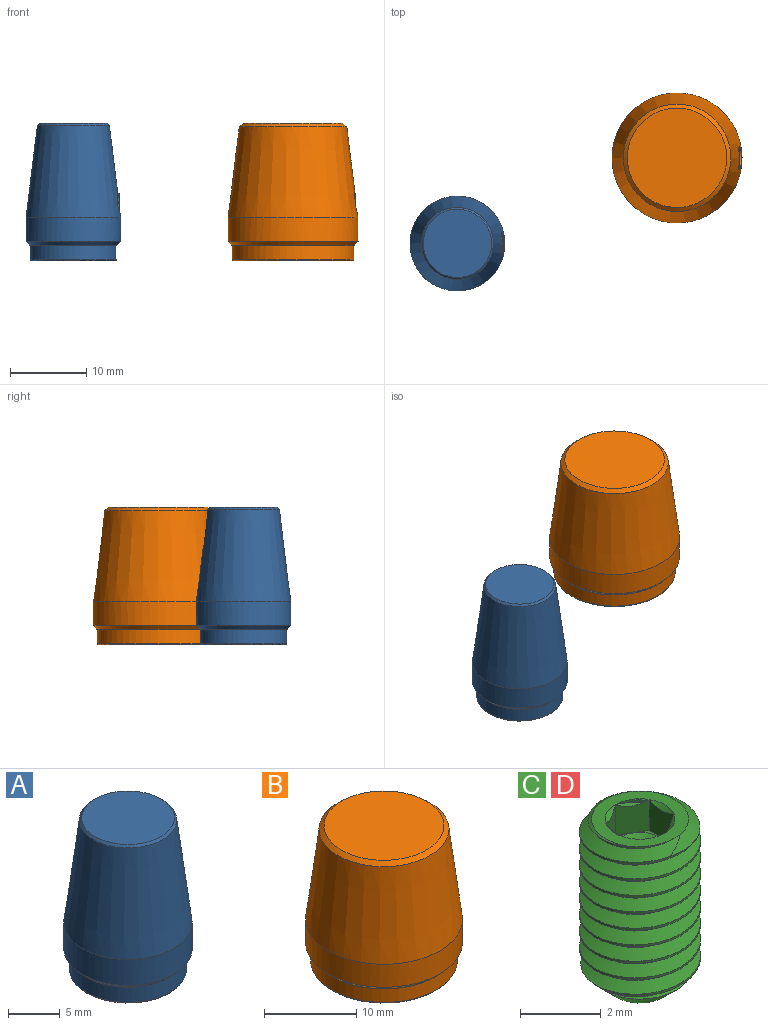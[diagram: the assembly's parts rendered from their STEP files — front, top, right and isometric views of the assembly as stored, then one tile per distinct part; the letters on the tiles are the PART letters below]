
ASSEMBLY  parts=4 mates=3
PART A: 20 faces, bbox 12.4x12.4x18 mm
  f0: cylinder r=1.61mm len=9.65mm, axis (0,0,-1), area 92.2mm2, adj f10,f12,f17
  f1: cone r=4.68mm half-angle=7deg, axis (0,0,-1), area 411.9mm2, adj f8,f11,f18
  f2: plane 8.96x8.96mm, normal (0,0,1), area 63mm2, adj f11
  f3: plane 1.22x1.22mm, normal (0,0,-1), area 1.2mm2, adj f10
  f4: plane 9.2x9.2mm, normal (0,0,-1), area 56.6mm2, adj f12,f13
  f5: cylinder r=4.75mm len=9.5mm, axis (0,0,-1), area 86.4mm2, adj f13,f14
  f6: plane 11x11mm, normal (0,0,-1), area 19.4mm2, adj f14,f15
  f7: cylinder r=5.65mm len=11.3mm, axis (0,0,-1), area 63.3mm2, adj f15,f16
  f8: cylinder r=6.2mm len=12.4mm, axis (0,0,-1), area 118.8mm2, adj f1,f9
  f9: cone r=5.65mm half-angle=45deg, axis (0,0,1), area 26.7mm2, adj f8,f16
  f10: cone r=0.61mm half-angle=45deg, axis (0,0,-1), area 9.9mm2, adj f0,f3
  f11: cone r=4.71mm half-angle=42.9deg, axis (0,0,-1), area 9.8mm2, adj f1,f2
  f12: torus R=1.76mm, axis (0,0,-1), area 2.5mm2, adj f0,f4
  f13: torus R=4.6mm, axis (0,0,-1), area 7.1mm2, adj f4,f5
  f14: torus R=4.9mm, axis (0,0,-1), area 7.2mm2, adj f5,f6
  f15: torus R=5.5mm, axis (0,0,-1), area 8.4mm2, adj f6,f7
  f16: torus R=5.8mm, axis (0,0,-1), area 4.3mm2, adj f7,f9
  f17: cylinder r=1.25mm len=3.69mm, axis (1,0,0), area 26.5mm2, adj f0,f19
  f18: cylinder r=1.55mm len=3.1mm, axis (1,0,0), area 11.2mm2, adj f1,f19
  f19: plane 3.1x3.1mm, normal (1,0,0), area 2.6mm2, adj f17,f18
PART B: 21 faces, bbox 17.5x17.5x18 mm
  f0: cone r=6.98mm half-angle=7deg, axis (0,0,-1), area 579.1mm2, adj f8,f11,f17
  f1: plane 13.02x13.02mm, normal (0,0,1), area 133mm2, adj f11
  f2: plane 1.22x1.22mm, normal (0,0,-1), area 1.2mm2, adj f10
  f3: cylinder r=1.61mm len=9.65mm, axis (0,0,-1), area 97.6mm2, adj f10,f12
  f4: plane 11.7x11.7mm, normal (0,0,-1), area 97.7mm2, adj f12,f13
  f5: cylinder r=6mm len=12mm, axis (0,0,-1), area 109.1mm2, adj f13,f14
  f6: plane 15.6x15.6mm, normal (0,0,-1), area 72.1mm2, adj f14,f15
  f7: cylinder r=7.95mm len=15.9mm, axis (0,0,-1), area 89.1mm2, adj f15,f16
  f8: cylinder r=8.5mm len=17mm, axis (0,0,-1), area 162.9mm2, adj f0,f9
  f9: cone r=7.95mm half-angle=45deg, axis (0,0,1), area 37mm2, adj f8,f16
  f10: cone r=0.61mm half-angle=45deg, axis (0,0,-1), area 9.9mm2, adj f2,f3
  f11: cone r=7.03mm half-angle=48.5deg, axis (0,0,-1), area 30mm2, adj f0,f1
  f12: torus R=1.76mm, axis (0,0,-1), area 2.5mm2, adj f3,f4
  f13: torus R=5.85mm, axis (0,0,-1), area 8.9mm2, adj f4,f5
  f14: torus R=6.15mm, axis (0,0,-1), area 9.1mm2, adj f5,f6
  f15: torus R=7.8mm, axis (0,0,-1), area 11.9mm2, adj f6,f7
  f16: torus R=8.1mm, axis (0,0,-1), area 6mm2, adj f7,f9
  f17: cylinder r=1.55mm len=3.1mm, axis (1,0,0), area 11.1mm2, adj f0,f19
  f18: cylinder r=1.25mm len=4mm, axis (1,0,0), area 31.4mm2, adj f19,f20
  f19: plane 3.1x3.1mm, normal (1,0,0), area 2.6mm2, adj f17,f18
  f20: cone r=0mm half-angle=59deg, axis (1,0,0), area 5.7mm2, adj f18
PART C: 27 faces, bbox 3.3x3.8x5.5 mm
  f0: cone r=0.75mm half-angle=60deg, axis (0,0,1), area 2mm2, adj f6,f7,f8,f9,f10,f20
  f1: cone r=0.87mm half-angle=45deg, axis (0,0,1), area 0.1mm2, adj f11,f25
  f2: cone r=1664.28mm half-angle=59deg, axis (0,0,-1), area 2.5mm2, adj f3
  f3: cone r=0.82mm half-angle=45deg, axis (0,0,1), area 5mm2, adj f2,f4,f12,f13,f14
  f4: cylinder r=1.5mm len=4.11mm, axis (0,0,1), area 4.8mm2, adj f3,f5,f12,f14
  f5: cone r=1.5mm half-angle=55deg, axis (0,0,-1), area 1.4mm2, adj f4,f11,f12,f14
  f6: plane 0.65x0.38mm, normal (0,0,1), area 0mm2, adj f0,f25,f26
  f7: plane 0.75x0.22mm, normal (0,0,1), area 0mm2, adj f0,f21,f26
  f8: plane 0.65x0.38mm, normal (0,0,1), area 0mm2, adj f0,f21,f22
  f9: plane 0.65x0.38mm, normal (0,0,1), area 0mm2, adj f0,f22,f23
  f10: plane 0.75x0.22mm, normal (0,0,1), area 0mm2, adj f0,f23,f24
  f11: plane 2.42x2.4mm, normal (0,0,1), area 2.1mm2, adj f1,f5,f12,f13,f14,f15,f16,f17
  f12: bspline ~4.94x3.46mm, area 27.6mm2, adj f3,f4,f5,f11,f13
  f13: bspline ~4.77x2.35mm, area 4.3mm2, adj f3,f11,f12,f14
  f14: bspline ~4.83x3mm, area 27.6mm2, adj f3,f4,f5,f11,f13
  f15: cone r=0.87mm half-angle=45deg, axis (0,0,1), area 0mm2, adj f11,f21
  f16: cone r=0.87mm half-angle=45deg, axis (0,0,1), area 0mm2, adj f11,f22
  f17: cone r=0.87mm half-angle=45deg, axis (0,0,1), area 0mm2, adj f11,f23
  f18: cone r=0.87mm half-angle=45deg, axis (0,0,1), area 0mm2, adj f11,f24
  f19: cone r=0.87mm half-angle=45deg, axis (0,0,1), area 0mm2, adj f11,f26
  f20: plane 0.65x0.38mm, normal (0,0,1), area 0mm2, adj f0,f24,f25
  f21: plane 1.27x1.08mm, normal (0.5,-0.87,0), area 0.7mm2, adj f7,f8,f15,f22,f26
  f22: plane 1.27x1.19mm, normal (1,0,0), area 0.7mm2, adj f8,f9,f16,f21,f23
  f23: plane 1.27x1.08mm, normal (0.5,0.87,0), area 0.7mm2, adj f9,f10,f17,f22,f24
  f24: plane 1.27x1.08mm, normal (-0.5,0.87,0), area 0.7mm2, adj f10,f18,f20,f23,f25
  f25: plane 1.02x0.95mm, normal (-1,0,0), area 0.7mm2, adj f1,f6,f20,f24,f26
  f26: plane 1.27x1.08mm, normal (-0.5,-0.87,0), area 0.7mm2, adj f6,f7,f19,f21,f25
PART D: same geometry as C
PLACE A t=(0,0,-0.04)mm
PLACE B t=(28.75,11.2,-0.04)mm
PLACE C rot(axis=(0,1,0),90deg) t=(3.75,0,7.56)mm
PLACE D rot(axis=(0,1,0),90deg) t=(34.72,11.2,7.56)mm
MATE slider C.f1 <-> A.f17  axis (1,0,0) through (6,0,7.56)mm
MATE slider D.f1 <-> B.f17  axis (1,0,0) through (36.97,11.2,7.56)mm
MATE planar B.f0 <-> A.f0  axis (0,0,-1) through (28.75,11.2,-0.04)mm
